# Revit family: Plumbing_Fixtures_Grohe_Rainshower_Cosmo_Head_Shower_28368000_14_METRIC
name_source: partatom
category: Plumbing Fixtures
revit_build: Autodesk Revit 2014 (Build: 20130308_1515(x64)
units: mm (PartAtom-declared; Revit-internal decimal feet)

## types (1)
- Rainshower 28368000
    ADA Compliant = No
    Assembly Code = C1030220
    AssetType = Fixed
    CW Connection = Yes
    CWFU = 5
    ClassificationName = Uniclass2015
    ClassificationValue = Pr_40_20_87_76
    Cold Water Connection Diameter = 10 mm  [stored 0.0328084 ft]
    Cold Water Radius = 5 mm  [stored 0.0164042 ft]
    Color = Chrome
    Cost = 0 $
    Default Elevation = 600 mm
    Description = For maximum showering comfort and enjoyment choose a GROHE Rainshower® system. Our wide choice of feature-packed designs ensures theres a system to suit all personal showering habits, style preferences and installation scenarios. All models feature GROHE DreamSpray®  for perfect water distribution to every nozzle, while GROHE CoolTouch® technology ensures the outer surface is never too hot to touch.  Combining a Rainshower® head shower and a Sena hand shower, the luxurious systems are easy to install and feature the functionality of either a thermostat or a diverter. For the ultimate experience, Rainshower® systems with adjustable body jets deliver tailor-made showering for all family members whatever their height is.
    DocumentationCertificates = http://www.grohe.com
    DocumentationInstallationGuide = http://www.grohe.com
    DocumentationLiterature = http://cdn08.grohe.com
    DocumentationMaintenance = http://cdn08.grohe.com
    DocumentationTechnical = http://cdn08.grohe.com
    DurationUnit = Years
    Ecojoy = Yes
    ExpectedLife = 0
    Finish = Chrome
    Flow Pressure = min 0.5 bar/recommended 1 - 5 bar
    Flow Pressure Diagram = http://projects.grohe.com
    Flow Rate - Hand Shower = 12 L/min
    Flow Rate - Head Shower = 14.5 L/min
    HW Connection = Yes
    HWFU = 5
    Height = 1060 mm  [stored 3.47769 ft]
    Hot Water Connection Diameter = 10 mm  [stored 0.0328084 ft]
    Hot Water Radius = 5 mm  [stored 0.0164042 ft]
    Keynote = N13
    Length = 588 mm  [stored 1.92913 ft]
    Low Emitting Material = No
    Manufacturer = Grohe AG
    Material = Chrome
    Mixing Leaver = Yes
    Model = Rainshower 27 032 001
    ModelNumber = 28368000
    NBSDescription = Shower heads
    NBSObjectName = Shower heads
    NBSReference = 45-35-70/333
    Name = Rainshower 27 032 001
    Operating Pressure = max 10 bar
    Percentage of Recycled Content = 0
    Product Documentation Link = http://www.grohe.com
    Product Page URL = http://projects.grohe.com
    ProductionYear = 2015
    Safety Stop = 38°C
    Spare Parts List = http://projects.grohe.com
    Temp - Hot Water Supply = max 80°C
    Temp - Hot Water Supply (Recommended) = 60°C
    Test Pressure = 16 bar
    Type Comments = Shower system with thermostat for wall mounting consisting of: horizontal swivable 450 mm shower arm, exposed thermostat with Aquadimmer function, allows change between head shower, Rainshower modern (28 368) with ball, joint, turning angle 20° ± 20° and hand, shower Sena (28 034), adjustable in, height with gliding element (12 140), diverter: bath/shower, metal shower hose 1750 mm
    TypeName = Shower system with thermostat for wall mounting consisting of: horizontal swivable 450 mm shower arm, exposed thermostat with Aquadimmer function, allows change between head shower, Rainshower modern (28 368) with ball, joint, turning angle 20° ± 20° and hand, shower Sena (28 034), adjustable in, height with gliding element (12 140), diverter: bath/shower, metal shower hose 1750 mm
    URL = www.grohe.com
    Vent Connection = No
    WFU = 0
    WarrantyDurationUnit = Years
    Waste Connection = No
    Width = 313 mm  [stored 1.0269 ft]
    _BIMspec_GUID = 0
    _current revision = 2
    _distributed by = www.bimstore.co.uk

note: [stored X ft] marks values corroborated as IEEE doubles in the binary element streams (Revit-internal decimal feet)

## geometry (parser evidence)
native form markers: Blend x2, Sweep x3
no freeform markers — native parametric forms only
